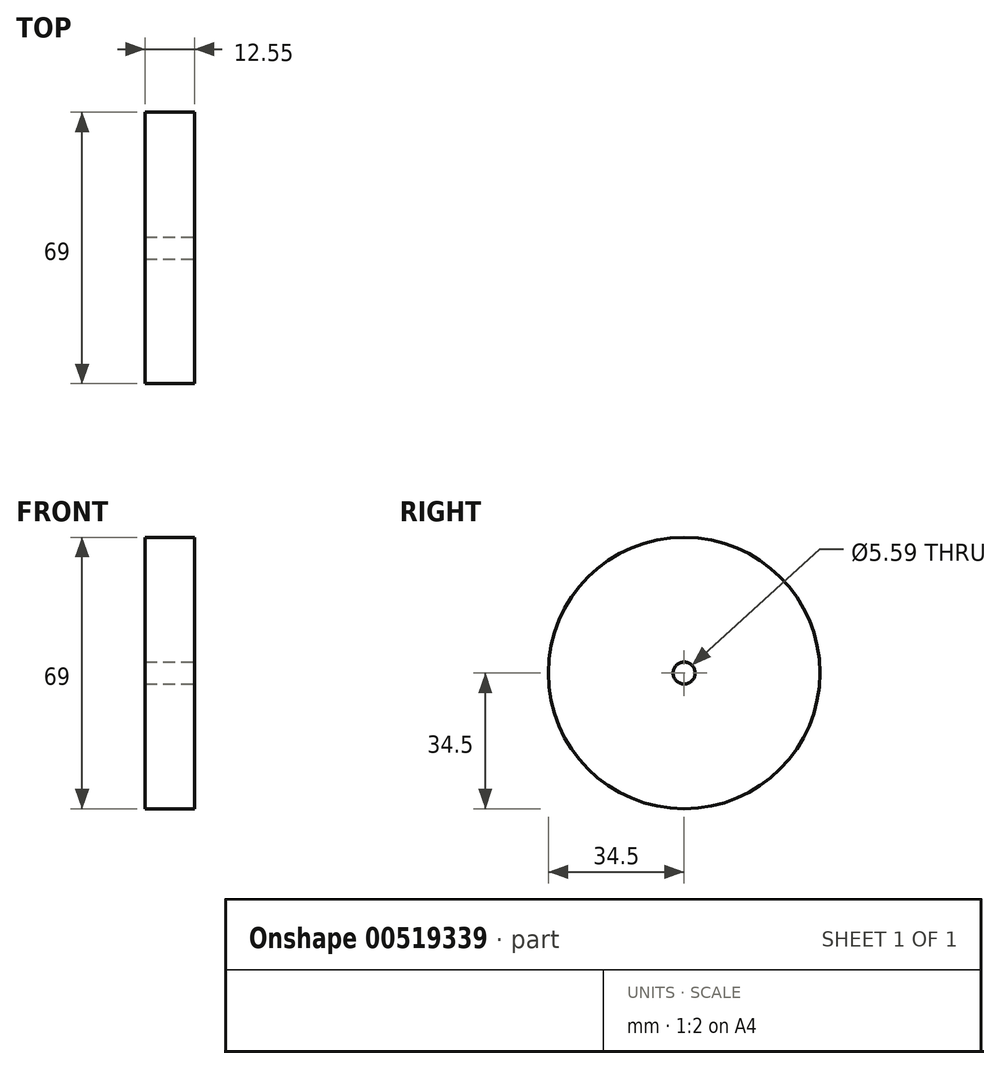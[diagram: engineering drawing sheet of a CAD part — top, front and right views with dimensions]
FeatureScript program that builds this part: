
annotation { "Feature Type Name" : "Feature", "Feature Type Description" : "" }
export const myFeature = defineFeature(function(context is Context, id is Id, definition is map)
    precondition{}
    {
        {
            var Q0;
            Q0=qCreatedBy(makeId("Right.planeOp"),FACE);
            var sketch = newSketch(context, id + "F0", { "sketchPlane" : qUnion([Q0])});
            skCircle(sketch, "E0", {"center": v(0, 0) * mm, "radius": 34.5 * mm});
            skSolve(sketch);
        }
        {
            var Q0;
            Q0 = qSketchRegion(id + "F0", true);
            extrude(context, id + "F1", {"entities" : qUnion([Q0]), "depth" : 12.55 * mm, "offsetDistance" : 25.4 * mm});
        }
        {
            var Q0;
            Q0=makeQuery(id+"F1.opExtrude","CAP_FACE",FACE,{"disambiguationData":[OSD([sQuery(id+"F0.wireOp",EDGE,"E0")])],"isStart":false});
            var sketch = newSketch(context, id + "F2", { "sketchPlane" : qUnion([Q0])});
            skCircle(sketch, "E1", {"center": v(0, 0) * mm, "radius": 2.8 * mm});
            skSolve(sketch);
        }
        {
            var Q0;
            Q0=makeQuery(id+"F2.imprint","IMPRINT",FACE,{"disambiguationData":[TD([[makeQuery(id+"F2.imprint","IMPRINT",EDGE,{"derivedFrom":sQuery(id+"F2.wireOp",EDGE,"E1")}),1.0]])]});
            var Q1;
            Q1=sQuery(id+"F2.wireOp",EDGE,"E1");
            extrude(context, id + "F3", {"entities" : qUnion([Q0]), "operationType" : NewBodyOperationType.REMOVE, "surfaceEntities" : qUnion([Q1]), "endBound" : BoundingType.THROUGH_ALL, "oppositeDirection" : true, "depth" : 25.4 * mm, "offsetDistance" : 25.4 * mm});
        }
    });
